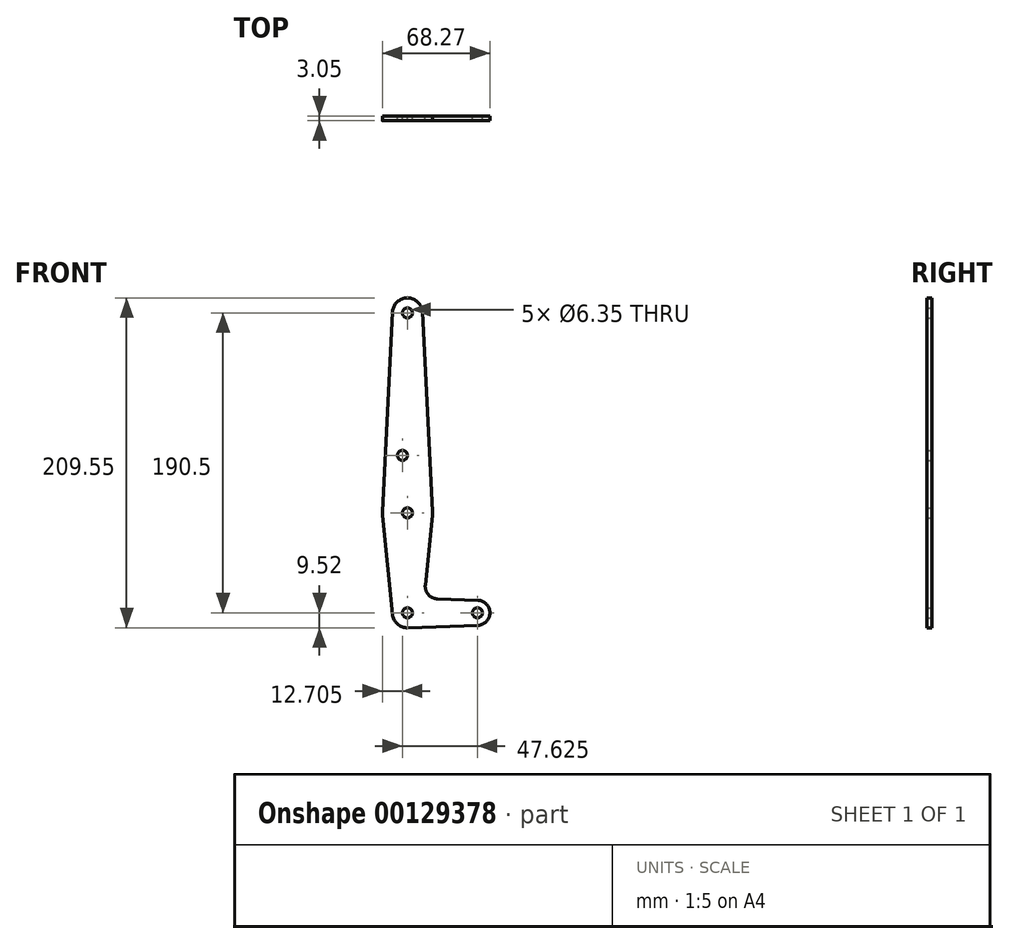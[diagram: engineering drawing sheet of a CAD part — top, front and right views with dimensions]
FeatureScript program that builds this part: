
annotation { "Feature Type Name" : "Feature", "Feature Type Description" : "" }
export const myFeature = defineFeature(function(context is Context, id is Id, definition is map)
    precondition{}
    {
        {
            var Q0;
            Q0=qCreatedBy(makeId("Front.planeOp"),FACE);
            var sketch = newSketch(context, id + "F0", { "sketchPlane" : qUnion([Q0])});
            skCircle(sketch, "E0", {"center": v(0, 190.5) * mm, "radius": 9.53 * mm});
            skCircle(sketch, "E1", {"center": v(0, 63.5) * mm, "radius": 15.88 * mm});
            skCircle(sketch, "E2", {"center": v(0, 0) * mm, "radius": 9.53 * mm});
            skCircle(sketch, "E3", {"center": v(44.45, 0) * mm, "radius": 7.94 * mm});
            skLineSegment(sketch, "E4", {"start": v(0, 190.5) * mm, "end": v(0, 63.5) * mm, "construction": true});
            skLineSegment(sketch, "E5", {"start": v(0, 63.5) * mm, "end": v(0, 0) * mm, "construction": true});
            skLineSegment(sketch, "E6", {"start": v(0, 0) * mm, "end": v(44.45, 0) * mm, "construction": true});
            skLineSegment(sketch, "E7", {"start": v(-9.51, 190.98) * mm, "end": v(-15.86, 64.3) * mm});
            skLineSegment(sketch, "E8", {"start": v(-15.8, 61.91) * mm, "end": v(-9.48, -0.95) * mm});
            skLineSegment(sketch, "E9", {"start": v(9.51, 190.98) * mm, "end": v(15.86, 64.3) * mm});
            skLineSegment(sketch, "E10", {"start": v(15.8, 61.91) * mm, "end": v(11.34, 17.6) * mm});
            skLineSegment(sketch, "E11", {"start": v(18.97, 8.85) * mm, "end": v(44.73, 7.93) * mm});
            skLineSegment(sketch, "E12", {"start": v(0.34, -9.52) * mm, "end": v(44.73, -7.93) * mm});
            skCircle(sketch, "E13", {"center": v(0, 190.5) * mm, "radius": 3.17 * mm});
            skCircle(sketch, "E14", {"center": v(0, 63.5) * mm, "radius": 3.17 * mm});
            skCircle(sketch, "E15", {"center": v(0, 0) * mm, "radius": 3.17 * mm});
            skCircle(sketch, "E16", {"center": v(-3.17, 100.03) * mm, "radius": 3.17 * mm});
            skCircle(sketch, "E17", {"center": v(44.45, 0) * mm, "radius": 3.17 * mm});
            skArc(sketch, "E18.filletArc", {"start": v(11.34, 17.6) * mm, "mid": v(13.26, 11.57) * mm, "end": v(18.97, 8.85) * mm});
            skSolve(sketch);
        }
        {
            var Q0;
            Q0 = qSketchRegion(id + "F0", true);
            extrude(context, id + "F1", {"entities" : qUnion([Q0]), "depth" : 3.05 * mm});
        }
    });
